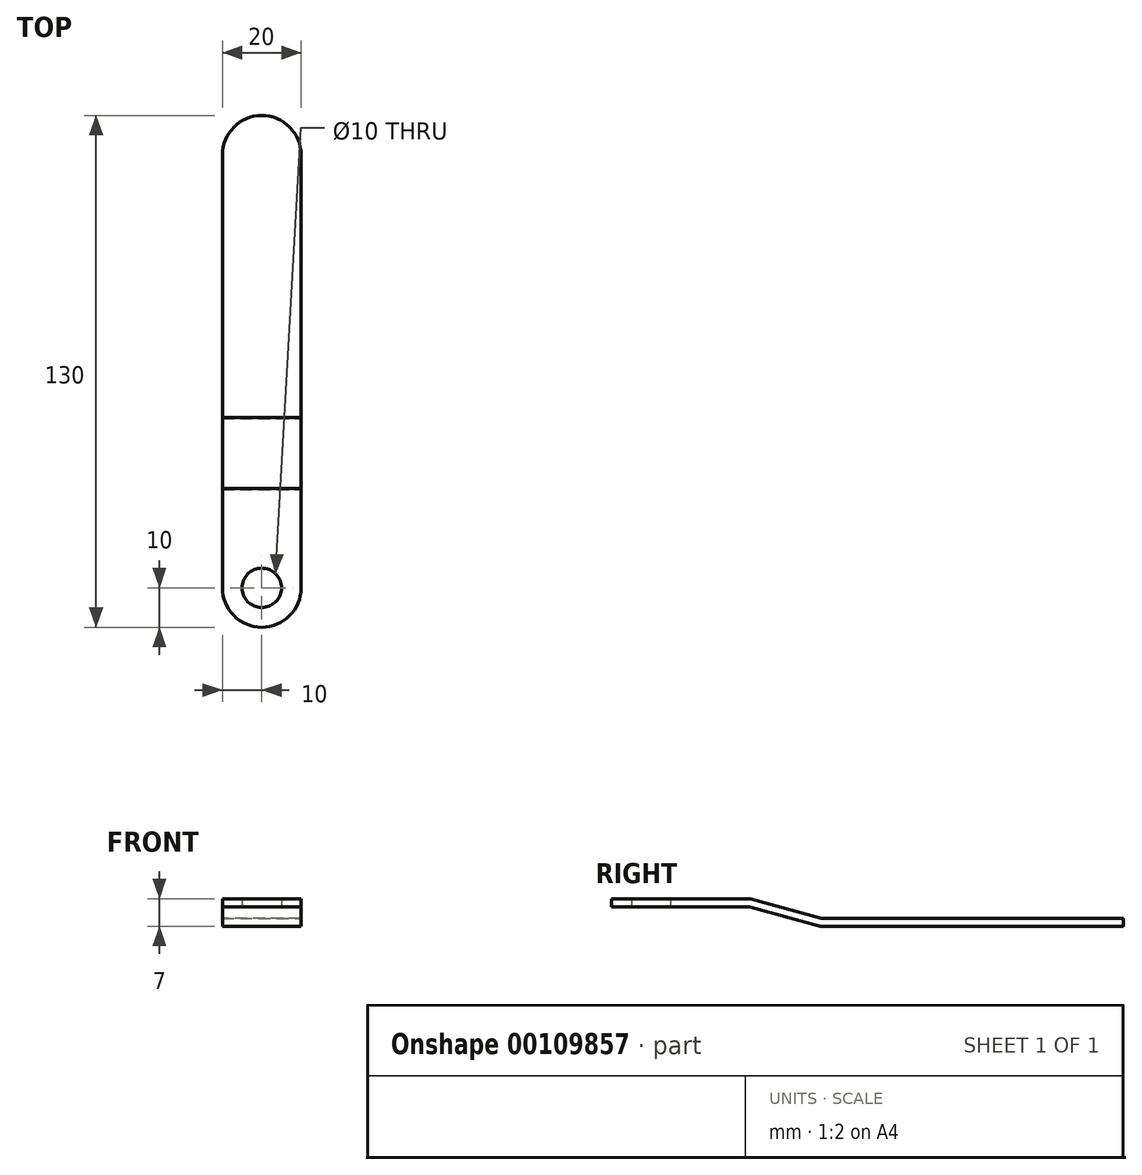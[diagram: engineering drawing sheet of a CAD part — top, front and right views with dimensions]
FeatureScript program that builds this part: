
annotation { "Feature Type Name" : "Feature", "Feature Type Description" : "" }
export const myFeature = defineFeature(function(context is Context, id is Id, definition is map)
    precondition{}
    {
        {
            var Q0;
            Q0=qCreatedBy(makeId("Top.planeOp"),FACE);
            var sketch = newSketch(context, id + "F0", { "sketchPlane" : qUnion([Q0])});
            skCircle(sketch, "E0", {"center": v(0, 0) * mm, "radius": 5 * mm});
            skArc(sketch, "E1", {"start": v(-10, 0) * mm, "mid": v(0, -10) * mm, "end": v(10, 0) * mm});
            skLineSegment(sketch, "E2", {"start": v(-10, 0) * mm, "end": v(-10, 110) * mm});
            skLineSegment(sketch, "E3", {"start": v(10, 110) * mm, "end": v(10, 0) * mm});
            skArc(sketch, "E4", {"start": v(-10, 110) * mm, "mid": v(0, 120) * mm, "end": v(10, 110) * mm});
            skSolve(sketch);
        }
        {
            var Q0;
            Q0=makeQuery(id+"F0.imprint","IMPRINT",FACE,{"disambiguationData":[TD([[makeQuery(id+"F0.imprint","IMPRINT",EDGE,{"derivedFrom":sQuery(id+"F0.wireOp",EDGE,"E0")}),-1.0]])]});
            extrude(context, id + "F1", {"entities" : qUnion([Q0]), "depth" : 7 * mm});
        }
        {
            var Q0;
            Q0=qCreatedBy(makeId("Right.planeOp"),FACE);
            var sketch = newSketch(context, id + "F2", { "sketchPlane" : qUnion([Q0])});
            skLineSegment(sketch, "E5", {"start": v(-10, 5) * mm, "end": v(25, 5) * mm});
            skLineSegment(sketch, "E6", {"start": v(25, 5) * mm, "end": v(43, 0) * mm});
            skLineSegment(sketch, "E7", {"start": v(43, 0) * mm, "end": v(120, 0) * mm});
            skLineSegment(sketch, "E8", {"start": v(120, 0) * mm, "end": v(120, 2) * mm});
            skLineSegment(sketch, "E9", {"start": v(120, 2) * mm, "end": v(43.27, 2) * mm});
            skLineSegment(sketch, "E10", {"start": v(43.27, 2) * mm, "end": v(25.27, 7) * mm});
            skLineSegment(sketch, "E11", {"start": v(25.27, 7) * mm, "end": v(-10, 7) * mm});
            skLineSegment(sketch, "E12", {"start": v(-10, 7) * mm, "end": v(-10, 5) * mm});
            skSolve(sketch);
        }
        {
            var Q0;
            Q0=qSketchRegion(id+"F2",true);
            extrude(context, id + "F3", {"entities" : qUnion([Q0]), "operationType" : NewBodyOperationType.INTERSECT, "endBound" : BoundingType.SYMMETRIC, "oppositeDirection" : true, "depth" : 20 * mm});
        }
    });
